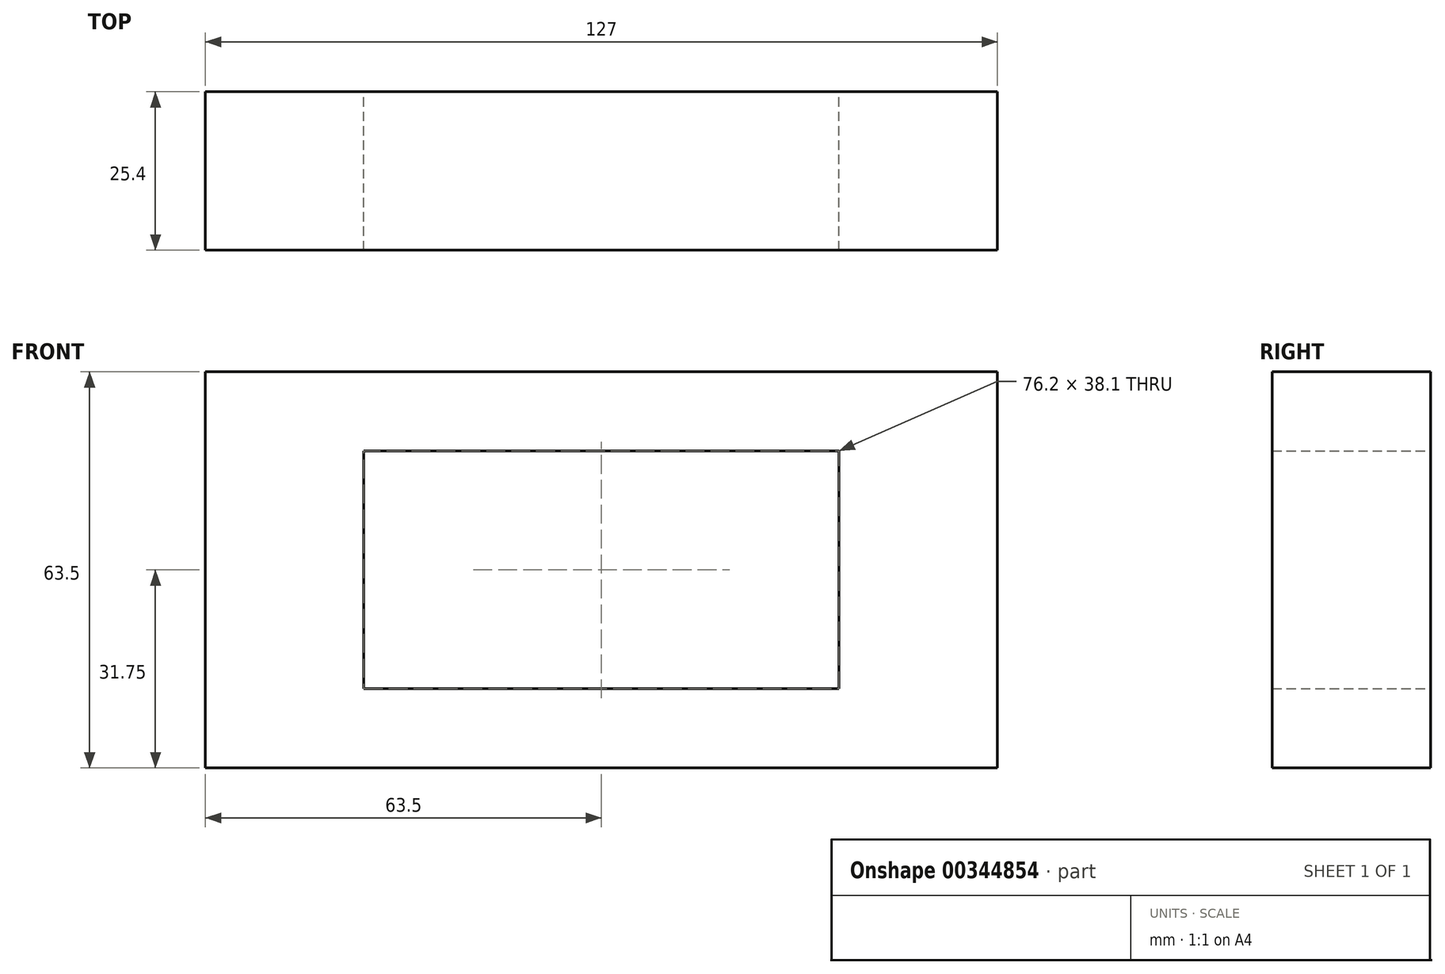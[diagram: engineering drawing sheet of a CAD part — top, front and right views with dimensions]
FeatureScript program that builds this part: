
annotation { "Feature Type Name" : "Feature", "Feature Type Description" : "" }
export const myFeature = defineFeature(function(context is Context, id is Id, definition is map)
    precondition{}
    {
        {
            var Q0;
            Q0=qCreatedBy(makeId("Front.planeOp"),FACE);
            var sketch = newSketch(context, id + "F0", { "sketchPlane" : qUnion([Q0])});
            skLineSegment(sketch, "E0.bottom", {"start": v(63.5, 31.75) * mm, "end": v(-63.5, 31.75) * mm});
            skLineSegment(sketch, "E0.top", {"start": v(63.5, -31.75) * mm, "end": v(-63.5, -31.75) * mm});
            skLineSegment(sketch, "E0.left", {"start": v(63.5, 31.75) * mm, "end": v(63.5, -31.75) * mm});
            skLineSegment(sketch, "E0.right", {"start": v(-63.5, 31.75) * mm, "end": v(-63.5, -31.75) * mm});
            skPoint(sketch, "E0.middle", {"position": v(0, 0) * mm});
            skLineSegment(sketch, "E1.bottom", {"start": v(38.1, 19.05) * mm, "end": v(-38.1, 19.05) * mm});
            skLineSegment(sketch, "E1.top", {"start": v(38.1, -19.05) * mm, "end": v(-38.1, -19.05) * mm});
            skLineSegment(sketch, "E1.left", {"start": v(38.1, 19.05) * mm, "end": v(38.1, -19.05) * mm});
            skLineSegment(sketch, "E1.right", {"start": v(-38.1, 19.05) * mm, "end": v(-38.1, -19.05) * mm});
            skSolve(sketch);
        }
        {
            var Q0;
            Q0 = qSketchRegion(id + "F0", true);
            extrude(context, id + "F1", {"entities" : qUnion([Q0]), "depth" : 25.4 * mm});
        }
    });
